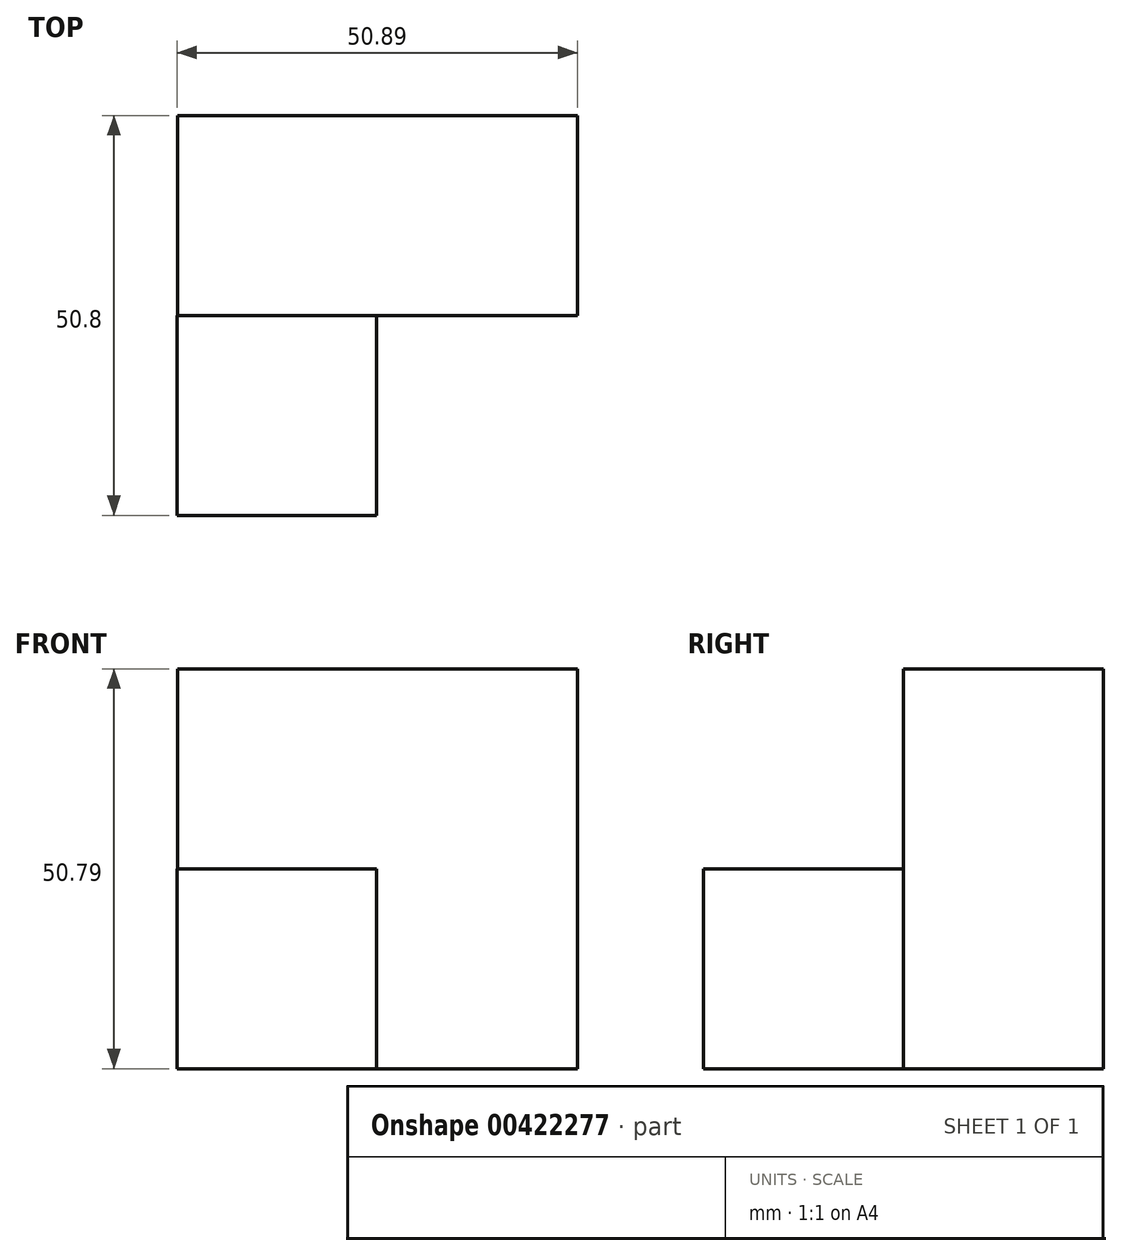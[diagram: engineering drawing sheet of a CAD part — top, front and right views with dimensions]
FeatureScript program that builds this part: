
annotation { "Feature Type Name" : "Feature", "Feature Type Description" : "" }
export const myFeature = defineFeature(function(context is Context, id is Id, definition is map)
    precondition{}
    {
        {
            var Q0;
            Q0=qCreatedBy(makeId("Front.planeOp"),FACE);
            var sketch = newSketch(context, id + "F0", { "sketchPlane" : qUnion([Q0])});
            skLineSegment(sketch, "E0.bottom", {"start": v(-76.38, -76) * mm, "end": v(-50.98, -76) * mm});
            skLineSegment(sketch, "E0.top", {"start": v(-76.38, -50.6) * mm, "end": v(-50.98, -50.6) * mm});
            skLineSegment(sketch, "E0.left", {"start": v(-76.38, -76) * mm, "end": v(-76.38, -50.6) * mm});
            skLineSegment(sketch, "E0.right", {"start": v(-50.98, -76) * mm, "end": v(-50.98, -50.6) * mm});
            skSolve(sketch);
        }
        {
            var Q0;
            Q0=qCreatedBy(makeId("Front.planeOp"),FACE);
            var sketch = newSketch(context, id + "F1", { "sketchPlane" : qUnion([Q0])});
            skLineSegment(sketch, "E1.bottom", {"start": v(-76.28, -76) * mm, "end": v(-25.49, -76) * mm});
            skLineSegment(sketch, "E1.top", {"start": v(-76.28, -25.2) * mm, "end": v(-25.49, -25.2) * mm});
            skLineSegment(sketch, "E1.left", {"start": v(-76.28, -76) * mm, "end": v(-76.28, -25.2) * mm});
            skLineSegment(sketch, "E1.right", {"start": v(-25.49, -76) * mm, "end": v(-25.49, -25.2) * mm});
            skSolve(sketch);
        }
        {
            var Q0;
            Q0=makeQuery(id+"F1.imprint","IMPRINT",FACE,{"disambiguationData":[TD([[makeQuery(id+"F1.imprint","IMPRINT",EDGE,{"derivedFrom":sQuery(id+"F1.wireOp",EDGE,"E1.bottom")}),1.0]])]});
            extrude(context, id + "F2", {"entities" : qUnion([Q0]), "depth" : -25.4 * mm});
        }
        {
            var Q0;
            Q0=makeQuery(id+"F0.imprint","IMPRINT",FACE,{"disambiguationData":[TD([[makeQuery(id+"F0.imprint","IMPRINT",EDGE,{"derivedFrom":sQuery(id+"F0.wireOp",EDGE,"E0.bottom")}),1.0]])]});
            extrude(context, id + "F3", {"entities" : qUnion([Q0]), "operationType" : NewBodyOperationType.ADD, "depth" : 25.4 * mm});
        }
    });
